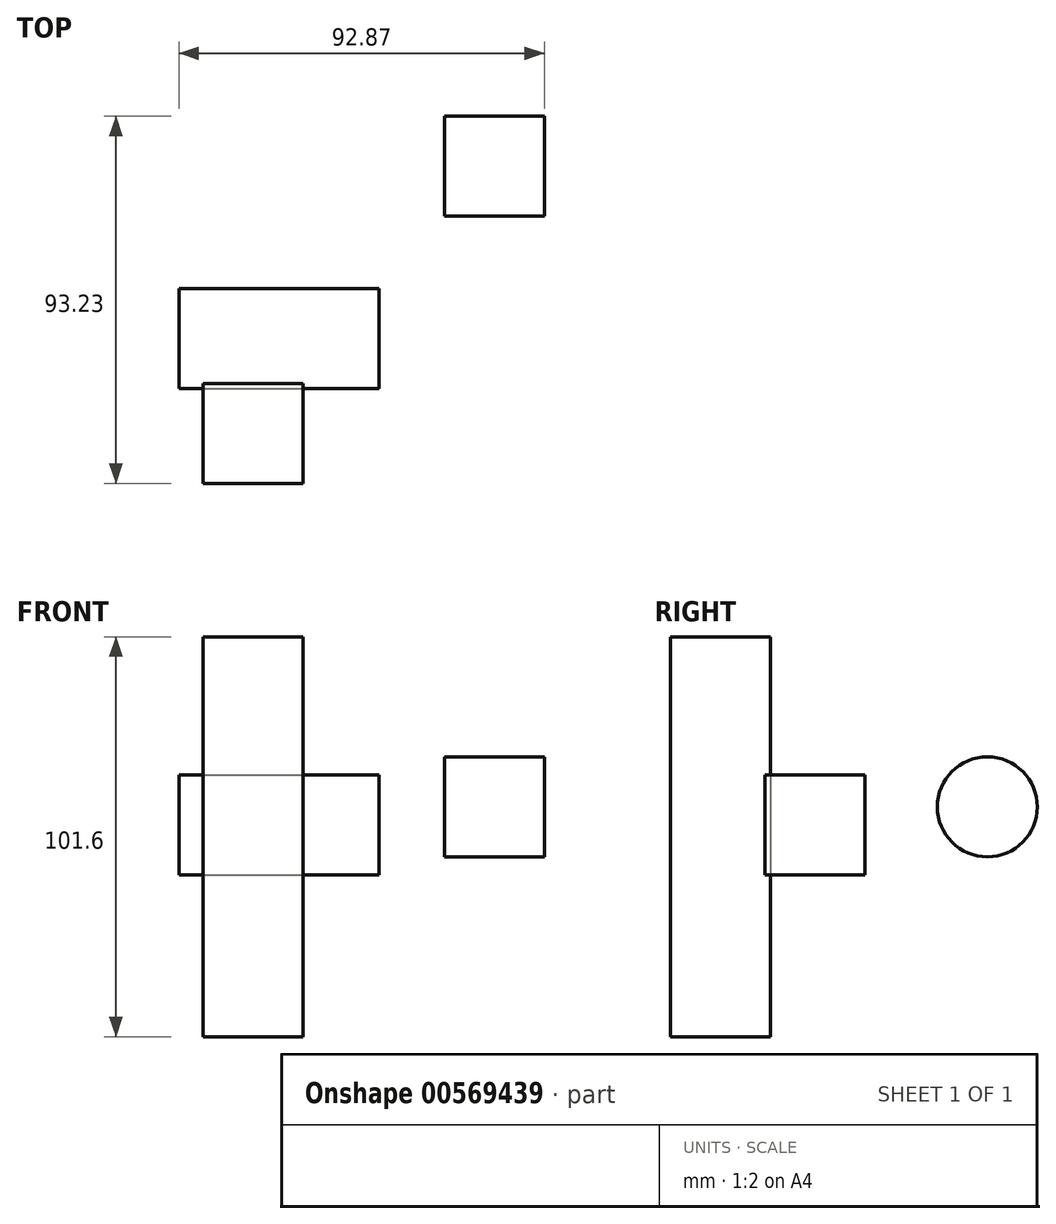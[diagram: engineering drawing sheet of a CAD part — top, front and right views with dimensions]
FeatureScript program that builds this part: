
annotation { "Feature Type Name" : "Feature", "Feature Type Description" : "" }
export const myFeature = defineFeature(function(context is Context, id is Id, definition is map)
    precondition{}
    {
        {
            var Q0;
            Q0=qCreatedBy(makeId("Front.planeOp"),FACE);
            var sketch = newSketch(context, id + "F0", { "sketchPlane" : qUnion([Q0])});
            skLineSegment(sketch, "E0.bottom", {"start": v(-67.47, 66.51) * mm, "end": v(-16.67, 66.51) * mm});
            skLineSegment(sketch, "E0.top", {"start": v(-67.47, 41.11) * mm, "end": v(-16.67, 41.11) * mm});
            skLineSegment(sketch, "E0.left", {"start": v(-67.47, 66.51) * mm, "end": v(-67.47, 41.11) * mm});
            skLineSegment(sketch, "E0.right", {"start": v(-16.67, 66.51) * mm, "end": v(-16.67, 41.11) * mm});
            skSolve(sketch);
        }
        {
            var Q0;
            Q0=makeQuery(id+"F0.imprint","IMPRINT",FACE,{"disambiguationData":[TD([[makeQuery(id+"F0.imprint","IMPRINT",EDGE,{"derivedFrom":sQuery(id+"F0.wireOp",EDGE,"E0.bottom")}),-1.0]])]});
            extrude(context, id + "F1", {"entities" : qUnion([Q0]), "depth" : 25.4 * mm, "offsetDistance" : 25.4 * mm});
        }
        {
            var Q0;
            Q0=qCreatedBy(makeId("Top.planeOp"),FACE);
            var sketch = newSketch(context, id + "F2", { "sketchPlane" : qUnion([Q0])});
            skLineSegment(sketch, "E1.bottom", {"start": v(-61.33, -49.44) * mm, "end": v(-35.93, -49.44) * mm});
            skLineSegment(sketch, "E1.top", {"start": v(-61.33, -24.04) * mm, "end": v(-35.93, -24.04) * mm});
            skLineSegment(sketch, "E1.left", {"start": v(-61.33, -49.44) * mm, "end": v(-61.33, -24.04) * mm});
            skLineSegment(sketch, "E1.right", {"start": v(-35.93, -49.44) * mm, "end": v(-35.93, -24.04) * mm});
            skSolve(sketch);
        }
        {
            var Q0;
            Q0=makeQuery(id+"F2.imprint","IMPRINT",FACE,{"disambiguationData":[TD([[makeQuery(id+"F2.imprint","IMPRINT",EDGE,{"derivedFrom":sQuery(id+"F2.wireOp",EDGE,"E1.bottom")}),1.0]])]});
            extrude(context, id + "F3", {"entities" : qUnion([Q0]), "depth" : 101.6 * mm, "offsetDistance" : 25.4 * mm});
        }
        {
            var Q0;
            Q0=qCreatedBy(makeId("Right.planeOp"),FACE);
            var sketch = newSketch(context, id + "F4", { "sketchPlane" : qUnion([Q0])});
            skCircle(sketch, "E2", {"center": v(31.09, 58.4) * mm, "radius": 12.7 * mm});
            skSolve(sketch);
        }
        {
            var Q0;
            Q0 = qSketchRegion(id + "F4", true);
            extrude(context, id + "F5", {"entities" : qUnion([Q0]), "depth" : 25.4 * mm, "offsetDistance" : 25.4 * mm});
        }
    });
